# Revit family: Workstations-Multi_Level-Teknion-BH_FB_Height_Adjustable_Desk_Bevel_Base-R2019
name_source: partatom
category: Furniture
units: mm (PartAtom-declared; Revit-internal decimal feet)

## family parameters
Always vertical = Yes
Cut with Voids When Loaded = No
OmniClass Number = 23.40.20.00
OmniClass Title = General Furniture and Specialties
Room Calculation Point = No
Shared = Yes
Work Plane-Based = No

## types (6) — shared parameters
Assembly Code = E2020200
Manufacturer = Teknion
Manufacturer Fax = 416.661.4586
Part Number = BH_FB
Product Documentation Link = https://www.teknion.com
Product Documentation Link #2 = http://www.teknion.com
Product Documentation Link #3 = http://www.teknion.com
Product Documentation Link #4 = http://www.teknion.com
Product Documentation Link #5 = http://www.teknion.com
Product Line = Expansion Casegoods
Product Page URL = https://www.teknion.com
Series = Expansion Casegoods
Sustainability Data = https://www.teknion.com
URL = www.teknion.com
Unit Weight URL = http://www.teknion.com
Warranty = http://www.teknion.com

## per-type parameters (varying)
| type | Description | Integrated Powerbar | Integrated Powerbar with IEC Outlet | Model | Shared Outlets for Regular Powebar and IEC Powerbar | Side Panel Thickness | Worksurface Thickness |
| 1 3/16" WS Thickness, 29" Depth, Integrated Powerbar | Height-Adjustable Desk - Bevel Bases, 1 3/16" Worksurface Thickness, 29" Depth, Integrated Powerbar, Extended Range 26" to 28" | Yes | No | BHMFB29___IE | Yes | 1.016 " | 1.193 " |
| 1 9/16" WS Thickness, 29" Depth, Integrated Powerbar | Height-Adjustable Desk - Bevel Bases, 1 9/16" Worksurface Thickness, 29" Depth, Integrated Powerbar, Extended Range 26" to 28" | Yes | No | BHXFB29___IE | Yes | 1.555 " | 1.555 " |
| 1 3/16" WS Thickness, 29" Depth, Integrated Powerbar with IEC Outlet | Height-Adjustable Desk - Bevel Bases, 1 3/16" Worksurface Thickness, 29" Depth, Integrated Powerbar with IEC Outlet, Extended Range 26" to 28" | No | Yes | BHMFB29___PE | Yes | 1.016 " | 1.193 " |
| 1 3/16" WS Thickness, 29" Depth, No Powerbar | Height-Adjustable Desk - Bevel Bases, 1 3/16" Worksurface Thickness, 29" Depth, No Powerbar, Extended Range 26" to 28" | No | No | BHMFB29___NE | No | 1.016 " | 1.193 " |
| 1 9/16" WS Thickness, 29" Depth, Integrated Powerbar with IEC Outlet | Height-Adjustable Desk - Bevel Bases, 1 9/16" Worksurface Thickness, 29" Depth, Integrated Powerbar with IEC Outlet, Extended Range 26" to 28" | No | Yes | BHXFB29___PE | Yes | 1.555 " | 1.555 " |
| 1 9/16" WS Thickness, 29" Depth, No Powerbar | Height-Adjustable Desk - Bevel Bases, 1 9/16" Worksurface Thickness, 29" Depth, No Powerbar, Extended Range 26" to 28" | No | No | BHXFB29___NE | No | 1.555 " | 1.555 " |

## geometry (parser evidence)
native form markers: Blend x6, Sweep x2
no freeform markers — native parametric forms only
